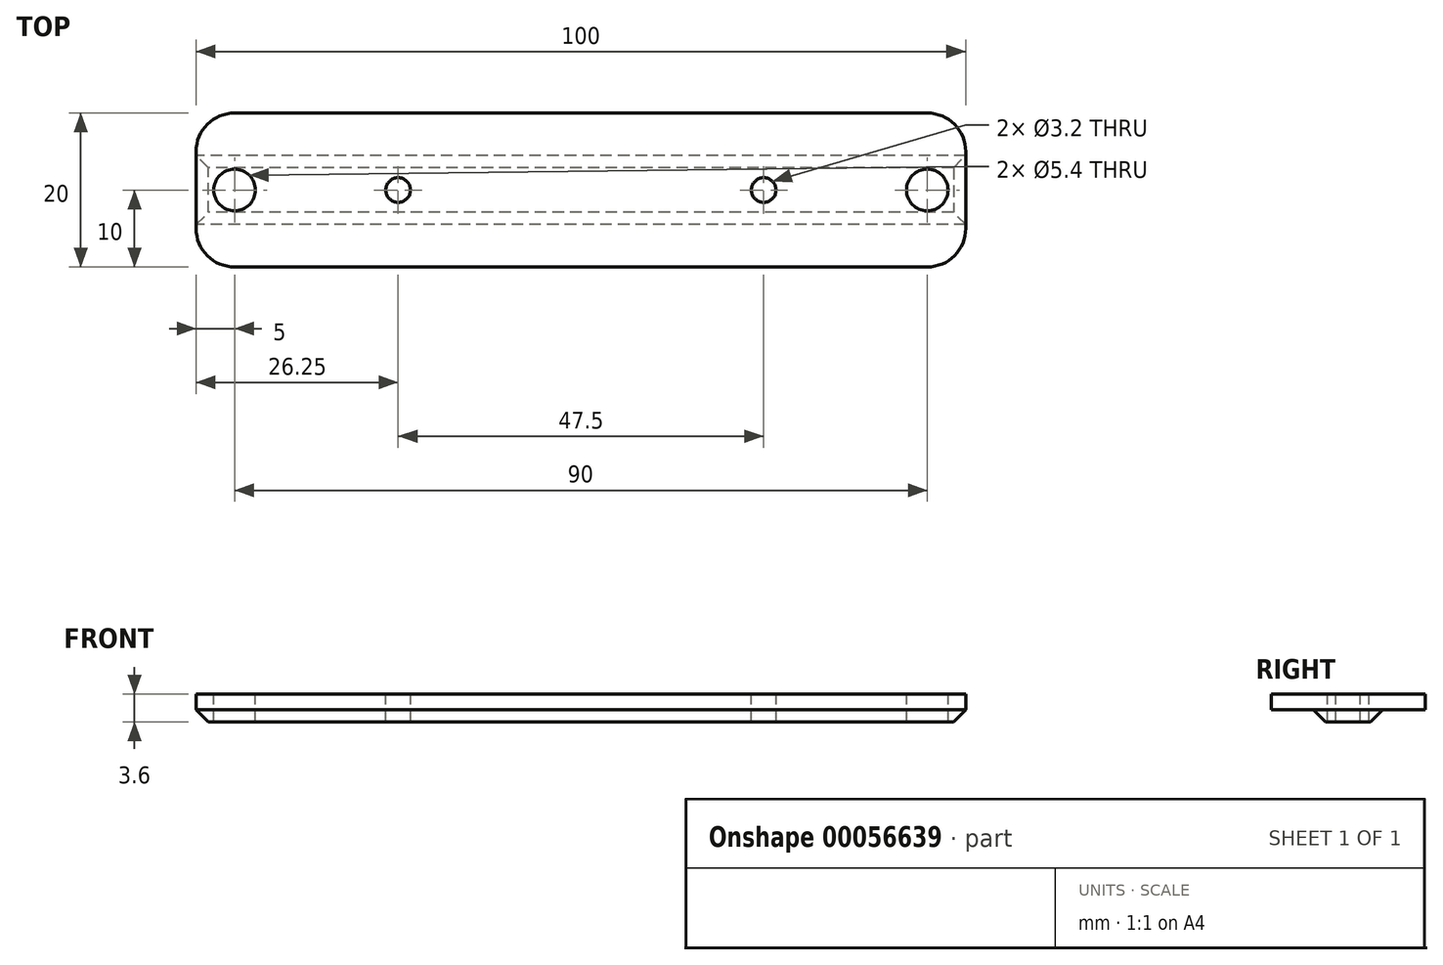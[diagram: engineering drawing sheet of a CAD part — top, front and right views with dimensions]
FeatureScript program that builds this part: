
annotation { "Feature Type Name" : "Feature", "Feature Type Description" : "" }
export const myFeature = defineFeature(function(context is Context, id is Id, definition is map)
    precondition{}
    {
        {
            var Q0;
            Q0=qCreatedBy(makeId("Top.planeOp"),FACE);
            var sketch = newSketch(context, id + "F0", { "sketchPlane" : qUnion([Q0])});
            skLineSegment(sketch, "E0.rect.bottom", {"start": v(45, 10) * mm, "end": v(-45, 10) * mm});
            skLineSegment(sketch, "E0.rect.top", {"start": v(45, -10) * mm, "end": v(-45, -10) * mm});
            skLineSegment(sketch, "E0.rect.left", {"start": v(50, 5) * mm, "end": v(50, -5) * mm});
            skLineSegment(sketch, "E0.rect.right", {"start": v(-50, 5) * mm, "end": v(-50, -5) * mm});
            skPoint(sketch, "E0.rect.middle", {"position": v(0, 0) * mm});
            skPoint(sketch, "E1.visualSharp", {"position": v(-50, 10) * mm});
            skArc(sketch, "E1.filletArc", {"start": v(-45, 10) * mm, "mid": v(-48.54, 8.54) * mm, "end": v(-50, 5) * mm});
            skPoint(sketch, "E2.visualSharp", {"position": v(50, 10) * mm});
            skArc(sketch, "E2.filletArc", {"start": v(50, 5) * mm, "mid": v(48.54, 8.54) * mm, "end": v(45, 10) * mm});
            skPoint(sketch, "E3.visualSharp", {"position": v(50, -10) * mm});
            skArc(sketch, "E3.filletArc", {"start": v(45, -10) * mm, "mid": v(48.54, -8.54) * mm, "end": v(50, -5) * mm});
            skPoint(sketch, "E4.visualSharp", {"position": v(-50, -10) * mm});
            skArc(sketch, "E4.filletArc", {"start": v(-50, -5) * mm, "mid": v(-48.54, -8.54) * mm, "end": v(-45, -10) * mm});
            skSolve(sketch);
        }
        {
            var Q0;
            Q0 = qSketchRegion(id + "F0", true);
            extrude(context, id + "F1", {"entities" : qUnion([Q0]), "depth" : 2 * mm});
        }
        {
            var Q0;
            Q0=makeQuery(id+"F1.opExtrude","SWEPT_FACE",FACE,{"disambiguationData":[OSD([sQuery(id+"F0.wireOp",EDGE,"E0.rect.right")])]});
            var sketch = newSketch(context, id + "F2", { "sketchPlane" : qUnion([Q0])});
            skLineSegment(sketch, "E5", {"start": v(0, 0) * mm, "end": v(0, -1.6) * mm, "construction": true});
            skPoint(sketch, "E5.endSnap0", {"position": v(0, 0) * mm});
            skLineSegment(sketch, "E6", {"start": v(-2.9, -1.6) * mm, "end": v(2.9, -1.6) * mm});
            skLineSegment(sketch, "E7", {"start": v(-2.9, -1.6) * mm, "end": v(-4.5, 0) * mm});
            skLineSegment(sketch, "E8", {"start": v(-4.5, 0) * mm, "end": v(4.5, 0) * mm});
            skLineSegment(sketch, "E9", {"start": v(4.5, 0) * mm, "end": v(2.9, -1.6) * mm});
            skSolve(sketch);
        }
        {
            var Q0;
            Q0 = qSketchRegion(id + "F2", true);
            var Q1;
            Q1=makeQuery(id+"F1.opExtrude","SWEPT_FACE",FACE,{"disambiguationData":[OSD([sQuery(id+"F0.wireOp",EDGE,"E0.rect.left")])]});
            extrude(context, id + "F3", {"entities" : qUnion([Q0]), "operationType" : NewBodyOperationType.ADD, "endBound" : BoundingType.UP_TO_SURFACE, "oppositeDirection" : true, "endBoundEntityFace" : qUnion([Q1]), "depth" : 25 * mm});
        }
        {
            var Q0;
            Q0=makeQuery(id+"F1.opExtrude","CAP_FACE",FACE,{"disambiguationData":[OSD([sQuery(id+"F0.wireOp",EDGE,"E0.rect.bottom"),sQuery(id+"F0.wireOp",EDGE,"E0.rect.top"),sQuery(id+"F0.wireOp",EDGE,"E0.rect.left"),sQuery(id+"F0.wireOp",EDGE,"E0.rect.right"),sQuery(id+"F0.wireOp",EDGE,"E1.filletArc"),sQuery(id+"F0.wireOp",EDGE,"E2.filletArc"),sQuery(id+"F0.wireOp",EDGE,"E3.filletArc"),sQuery(id+"F0.wireOp",EDGE,"E4.filletArc")])],"isStart":false});
            var sketch = newSketch(context, id + "F4", { "sketchPlane" : qUnion([Q0])});
            skLineSegment(sketch, "E10", {"start": v(-50, 0) * mm, "end": v(-45, 0) * mm, "construction": true});
            skLineSegment(sketch, "E11", {"start": v(-45, 0) * mm, "end": v(-23.75, 0) * mm, "construction": true});
            skLineSegment(sketch, "E12", {"start": v(-23.75, 0) * mm, "end": v(0, 0) * mm, "construction": true});
            skLineSegment(sketch, "E13", {"start": v(0, 0) * mm, "end": v(23.75, 0) * mm, "construction": true});
            skLineSegment(sketch, "E14", {"start": v(23.75, 0) * mm, "end": v(45, 0) * mm, "construction": true});
            skLineSegment(sketch, "E15", {"start": v(45, 0) * mm, "end": v(50, 0) * mm, "construction": true});
            skCircle(sketch, "E16", {"center": v(-45, 0) * mm, "radius": 2.7 * mm});
            skCircle(sketch, "E17", {"center": v(45, 0) * mm, "radius": 2.7 * mm});
            skCircle(sketch, "E18", {"center": v(23.75, 0) * mm, "radius": 1.6 * mm});
            skCircle(sketch, "E19", {"center": v(-23.75, 0) * mm, "radius": 1.6 * mm});
            skSolve(sketch);
        }
        {
            var Q0;
            Q0 = qSketchRegion(id + "F4", true);
            extrude(context, id + "F5", {"entities" : qUnion([Q0]), "operationType" : NewBodyOperationType.REMOVE, "endBound" : BoundingType.THROUGH_ALL, "oppositeDirection" : true, "depth" : 25 * mm});
        }
        {
            var Q0;
            Q0=makeQuery(id+"F3.opExtrude","CAP_EDGE",EDGE,{"disambiguationData":[OSD([sQuery(id+"F2.wireOp",EDGE,"E6")])],"isStart":true});
            var Q1;
            Q1=makeQuery(id+"F3.opExtrude","CAP_EDGE",EDGE,{"disambiguationData":[OSD([sQuery(id+"F2.wireOp",EDGE,"E6")])],"isStart":false});
            chamfer(context, id + "F6", {"entities" : qUnion([Q0, Q1]), "width" : 1.6 * mm, "tangentPropagation" : true});
        }
    });
